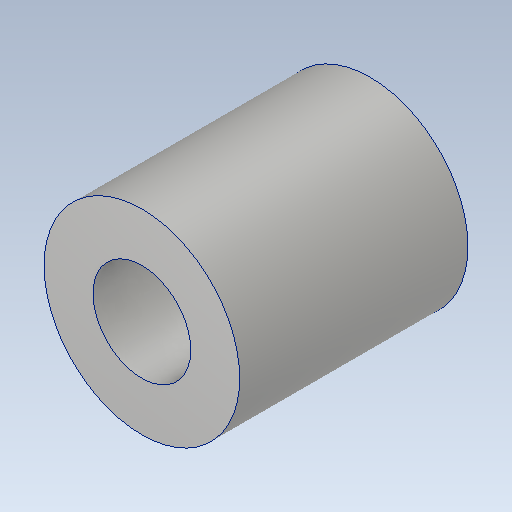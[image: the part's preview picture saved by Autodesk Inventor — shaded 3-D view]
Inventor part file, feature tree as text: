
AUTODESK INVENTOR PART (.ipt)
format: ipt  version: 2020.2 (Build 242310000, 310)  size: 113,664 bytes
history: native  units: mm
features: other x1, extrude x1, sketch x1
ambient origin geometry x8: Origin, YZ Plane, XZ Plane, XY Plane, X Axis, Y Axis, Z Axis, Center Point
bodies: Body1 (feature_tree)
feature tree (3):
  other  "ソリッド1"
  extrude  "押し出し1"  Depth=6.0mm
  sketch  "スケッチ1"
